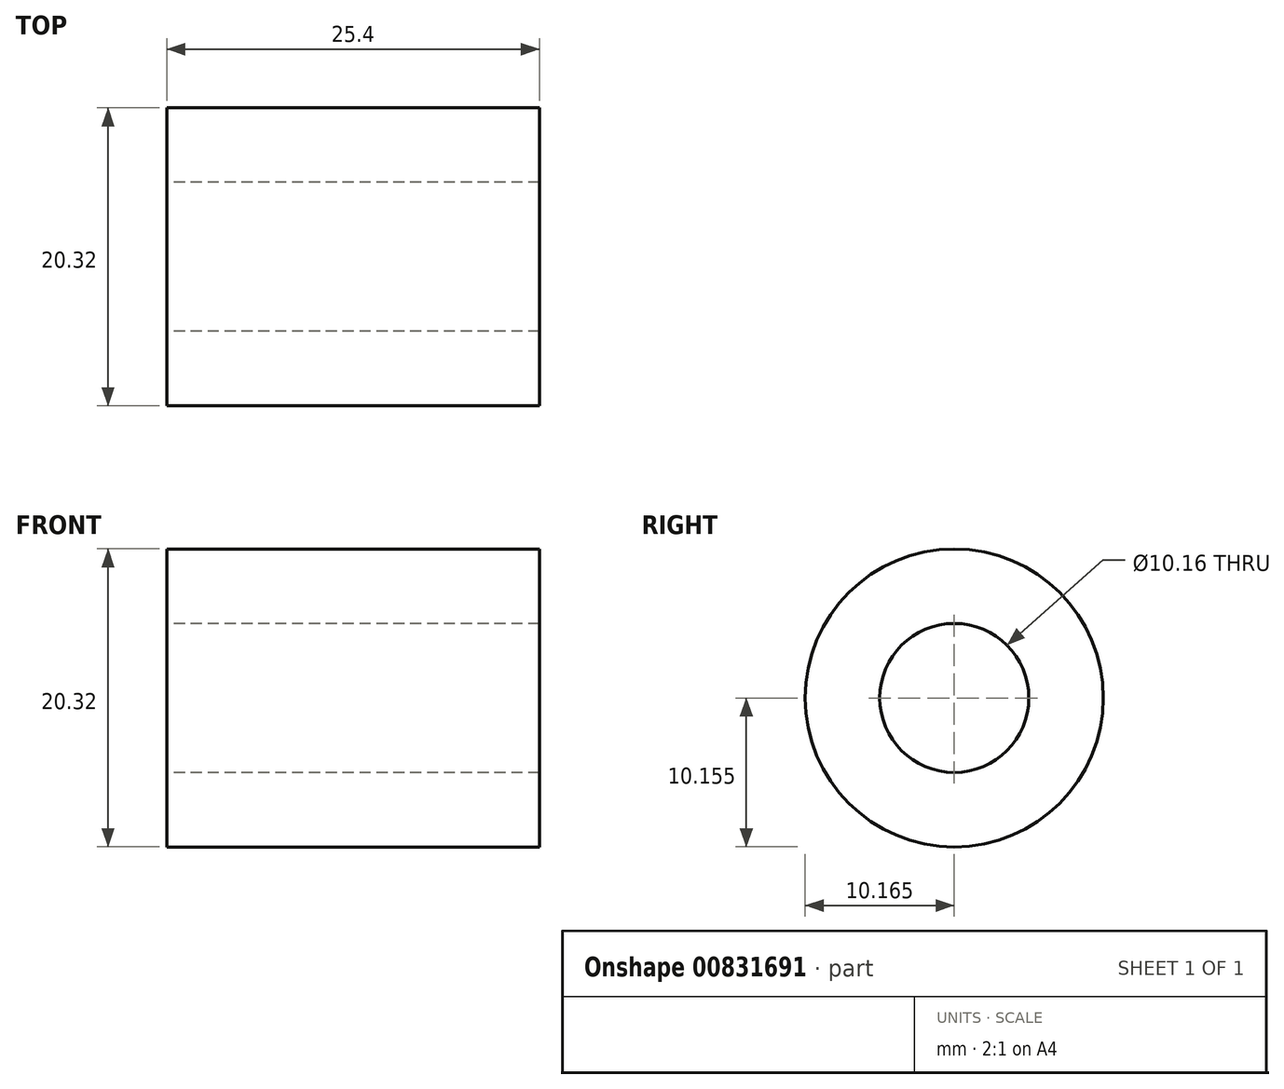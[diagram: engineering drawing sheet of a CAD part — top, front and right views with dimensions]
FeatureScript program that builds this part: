
annotation { "Feature Type Name" : "Feature", "Feature Type Description" : "" }
export const myFeature = defineFeature(function(context is Context, id is Id, definition is map)
    precondition{}
    {
        {
            var Q0;
            Q0=qCreatedBy(makeId("Right.planeOp"),FACE);
            var sketch = newSketch(context, id + "F0", { "sketchPlane" : qUnion([Q0])});
            skCircle(sketch, "E0", {"center": v(-6.82, 7.1) * mm, "radius": 10.16 * mm});
            skCircle(sketch, "E1", {"center": v(-6.82, 7.1) * mm, "radius": 5.08 * mm});
            skSolve(sketch);
        }
        {
            var Q0;
            Q0 = qSketchRegion(id + "F0", true);
            extrude(context, id + "F1", {"entities" : qUnion([Q0]), "depth" : 25.4 * mm, "offsetDistance" : 25.4 * mm});
        }
    });
